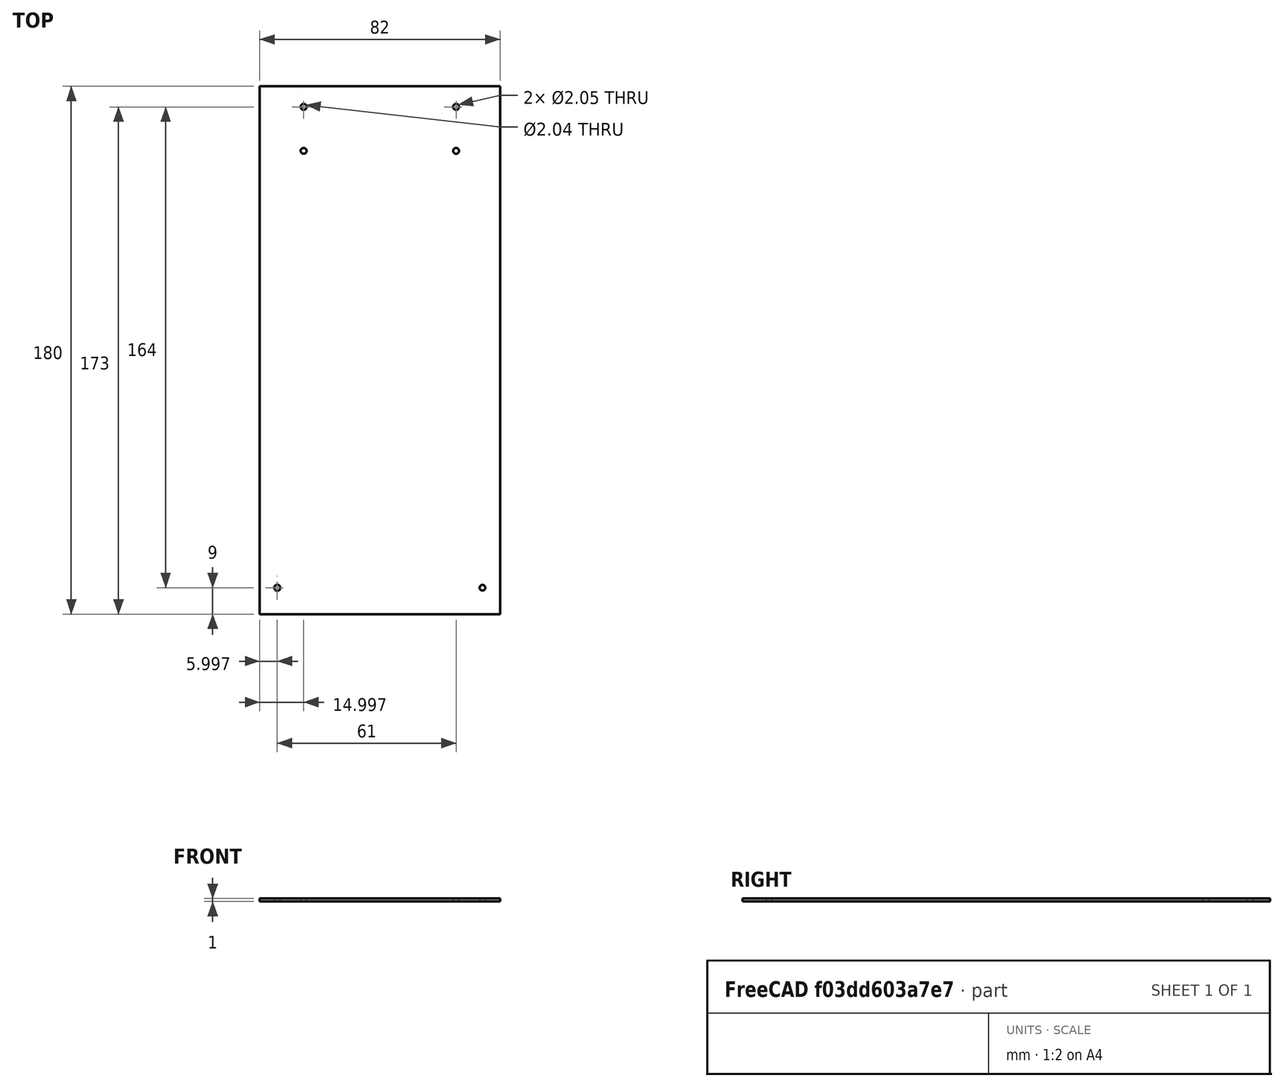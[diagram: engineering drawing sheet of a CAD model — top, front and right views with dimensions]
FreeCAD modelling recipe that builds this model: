
FCSTD DOCUMENT  (FreeCAD 0.19R24267 +148 (Git))
Label: BackWall
License: All rights reserved
LicenseURL: http://en.wikipedia.org/wiki/All_rights_reserved
objects: Sketcher::SketchObject×1, PartDesign::Pad×1, PartDesign::Body×1
note: 4 computed .brp shape members not serialized (recipe doc carries the construction recipe); baked Part::Feature solids carry a one-line shape summary decoded from their .brp

FEATURE [Sketcher::SketchObject] Sketch001  label="Back"
  FullyConstrained = false
  MapMode = 5
  Support = -> [XY_Plane]
  sketch-geometry (16):
    g0: LineSegment StartX=10.0967 StartY=-28.99 StartZ=0 EndX=92.0967 EndY=-28.99 EndZ=0
    g1: LineSegment StartX=92.0967 StartY=-28.99 StartZ=0 EndX=92.0967 EndY=-208.99 EndZ=0
    g2: LineSegment StartX=92.0967 StartY=-208.99 StartZ=0 EndX=10.0967 EndY=-208.99 EndZ=0
    g3: LineSegment StartX=10.0967 StartY=-208.99 StartZ=0 EndX=10.0967 EndY=-28.99 EndZ=0
    g4: GeomPoint X=25.0967 Y=-35.99 Z=0
    g5: GeomPoint X=25.0967 Y=-50.99 Z=0
    g6: GeomPoint X=77.0967 Y=-35.99 Z=0
    g7: GeomPoint X=77.0967 Y=-50.99 Z=0
    g8: GeomPoint X=16.0967 Y=-199.99 Z=0
    g9: GeomPoint X=86.0967 Y=-199.99 Z=0
    g10: Circle CenterX=77.0967 CenterY=-50.99 CenterZ=0 NormalX=0 NormalY=0 NormalZ=1 AngleXU=0 Radius=1.01045
    g11: Circle CenterX=77.0967 CenterY=-35.99 CenterZ=0 NormalX=0 NormalY=0 NormalZ=1 AngleXU=0 Radius=1.02628
    g12: Circle CenterX=25.0967 CenterY=-50.99 CenterZ=0 NormalX=0 NormalY=0 NormalZ=1 AngleXU=0 Radius=0.999289
    g13: Circle CenterX=25.0967 CenterY=-35.99 CenterZ=0 NormalX=0 NormalY=0 NormalZ=1 AngleXU=0 Radius=1.02236
    g14: Circle CenterX=16.0967 CenterY=-199.99 CenterZ=0 NormalX=0 NormalY=0 NormalZ=1 AngleXU=0 Radius=1.02636
    g15: Circle CenterX=86.0967 CenterY=-199.99 CenterZ=0 NormalX=0 NormalY=0 NormalZ=1 AngleXU=0 Radius=0.97078
  constraints (28):
    c: Coincident(g0,g1)
    c: Coincident(g1,g2)
    c: Coincident(g2,g3)
    c: Coincident(g3,g0)
    c: Horizontal(g0)
    c: Horizontal(g2)
    c: Vertical(g1)
    c: Vertical(g3)
    c: Distance(g0) = 82
    c: Distance(g1) = 180
    c: Vertical(g4,g5)
    c: Vertical(g6,g7)
    c: Distance(g4,g0) = 7
    c: Distance(g6,g0) = 7
    c: Distance(g4,g5) = 15
    c: Distance(g6,g7) = 15
    c: Distance(g4,g3) = 15
    c: Distance(g6,g1) = 15
    c: Distance(g8,g2) = 9
    c: Distance(g9,g2) = 9
    c: Distance(g8,g3) = 6
    c: Distance(g9,g1) = 6
    c: Coincident(g10,g7)
    c: Coincident(g11,g6)
    c: Coincident(g12,g5)
    c: Coincident(g13,g4)
    c: Coincident(g14,g8)
    c: Coincident(g15,g9)
FEATURE [PartDesign::Pad] Pad
  Direction = (1,1,1)
  Length = 1
  Length2 = 100
  Profile = -> Sketch001
  Type = 0
FEATURE [PartDesign::Body] Body
  Group = -> [Sketch001,Pad]
  Origin = -> Origin
  Tip = -> Pad
